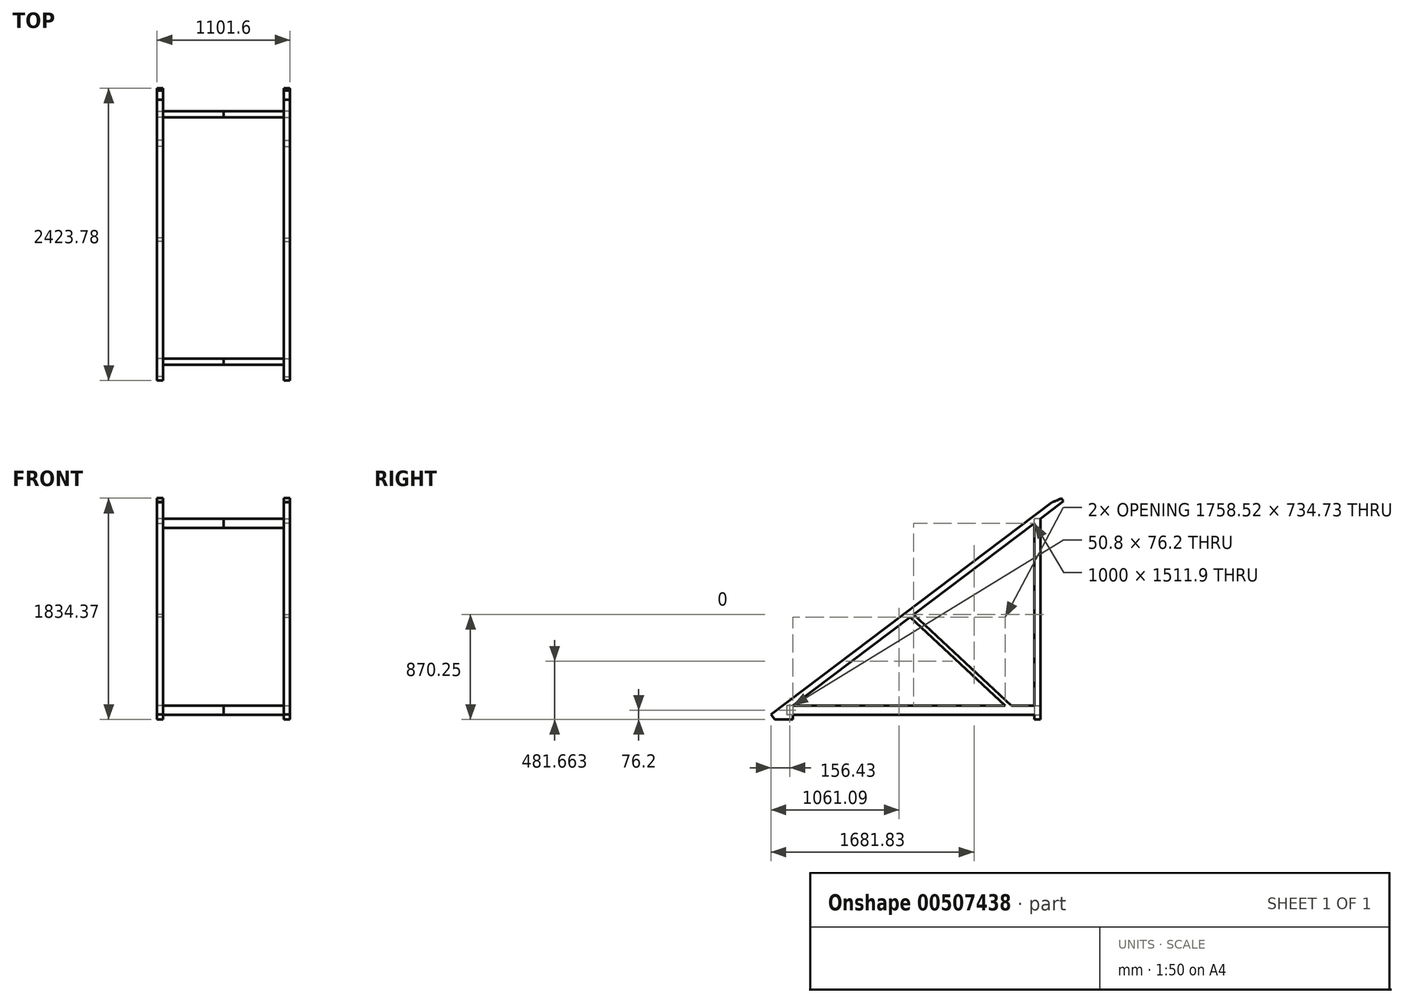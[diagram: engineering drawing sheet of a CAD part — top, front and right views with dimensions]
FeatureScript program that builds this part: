
annotation { "Feature Type Name" : "Feature", "Feature Type Description" : "" }
export const myFeature = defineFeature(function(context is Context, id is Id, definition is map)
    precondition{}
    {
        {
            var Q0;
            Q0=qCreatedBy(makeId("Front.planeOp"),FACE);
            var sketch = newSketch(context, id + "F0", { "sketchPlane" : qUnion([Q0])});
            skLineSegment(sketch, "E0.bottom", {"start": v(500, 0) * mm, "end": v(550.8, 0) * mm});
            skLineSegment(sketch, "E0.top", {"start": v(500, 76.2) * mm, "end": v(550.8, 76.2) * mm});
            skLineSegment(sketch, "E0.left", {"start": v(500, 0) * mm, "end": v(500, 76.2) * mm});
            skLineSegment(sketch, "E0.right", {"start": v(550.8, 0) * mm, "end": v(550.8, 76.2) * mm});
            skLineSegment(sketch, "E1", {"start": v(0, 0) * mm, "end": v(500, 0) * mm});
            skSolve(sketch);
        }
        {
            var Q0;
            Q0=qSketchRegion(id+"F0",true);
            extrude(context, id + "F1", {"entities" : qUnion([Q0]), "oppositeDirection" : true, "depth" : 2000 * mm});
        }
        {
            var Q0;
            Q0=makeQuery(id+"F1.opExtrude","CAP_FACE",FACE,{"disambiguationData":[OSD([sQuery(id+"F0.wireOp",EDGE,"E0.bottom"),sQuery(id+"F0.wireOp",EDGE,"E0.top"),sQuery(id+"F0.wireOp",EDGE,"E0.left"),sQuery(id+"F0.wireOp",EDGE,"E0.right")])],"isStart":false});
            var sketch = newSketch(context, id + "F2", { "sketchPlane" : qUnion([Q0])});
            skLineSegment(sketch, "E2", {"start": v(-550.8, 38.1) * mm, "end": v(-550.8, -38.1) * mm});
            skLineSegment(sketch, "E3", {"start": v(-550.8, -38.1) * mm, "end": v(-500, -38.1) * mm});
            skLineSegment(sketch, "E4", {"start": v(-500, -38.1) * mm, "end": v(-500, 38.1) * mm});
            skLineSegment(sketch, "E5.top", {"start": v(-550.8, 1588.1) * mm, "end": v(-500, 1588.1) * mm});
            skLineSegment(sketch, "E5.left", {"start": v(-550.8, 38.1) * mm, "end": v(-550.8, 1588.1) * mm});
            skLineSegment(sketch, "E5.right", {"start": v(-500, 38.1) * mm, "end": v(-500, 1588.1) * mm});
            skSolve(sketch);
        }
        {
            var Q0;
            Q0=qSketchRegion(id+"F2",true);
            extrude(context, id + "F3", {"entities" : qUnion([Q0]), "operationType" : NewBodyOperationType.ADD, "depth" : 50.8 * mm});
        }
        {
            var Q0;
            Q0=makeQuery(id+"F3.boolean.opBoolean","MERGE",FACE,{"derivedFrom":[makeQuery(id+"F1.opExtrude","SWEPT_FACE",FACE,{"disambiguationData":[OSD([sQuery(id+"F0.wireOp",EDGE,"E0.right")])]}),makeQuery(id+"F3.opExtrude","SWEPT_FACE",FACE,{"disambiguationData":[OSD([sQuery(id+"F2.wireOp",EDGE,"E2"),sQuery(id+"F2.wireOp",EDGE,"E5.left")])]})]});
            var sketch = newSketch(context, id + "F4", { "sketchPlane" : qUnion([Q0])});
            skLineSegment(sketch, "E6.0", {"start": v(2000, 76.2) * mm, "end": v(0, 76.2) * mm});
            skLineSegment(sketch, "E7.0", {"start": v(2000, 1588.1) * mm, "end": v(2000, 76.2) * mm});
            skLineSegment(sketch, "E8", {"start": v(-151.2, -38.1) * mm, "end": v(2241.95, 1771) * mm});
            skLineSegment(sketch, "E9", {"start": v(2241.95, 1771) * mm, "end": v(2000, 1588.1) * mm});
            skLineSegment(sketch, "E10.0", {"start": v(2050.8, -38.1) * mm, "end": v(2000, -38.1) * mm});
            skLineSegment(sketch, "E11", {"start": v(-151.2, -38.1) * mm, "end": v(0, -38.1) * mm});
            skPoint(sketch, "E12.0", {"position": v(2000, -19.05) * mm});
            skLineSegment(sketch, "E13.0", {"start": v(2000, 0) * mm, "end": v(2000, -38.1) * mm});
            skLineSegment(sketch, "E14", {"start": v(0, -38.1) * mm, "end": v(0, 0) * mm});
            skLineSegment(sketch, "E15", {"start": v(-151.2, -38.1) * mm, "end": v(-181.83, 2.42) * mm});
            skLineSegment(sketch, "E16", {"start": v(-181.83, 2.42) * mm, "end": v(2211.31, 1811.52) * mm});
            skLineSegment(sketch, "E17", {"start": v(2211.31, 1811.52) * mm, "end": v(2241.95, 1771) * mm});
            skLineSegment(sketch, "E18.0", {"start": v(2050.8, 1588.1) * mm, "end": v(2000, 1588.1) * mm});
            skLineSegment(sketch, "E19", {"start": v(2050.8, 1588.1) * mm, "end": v(2050.8, 1626.5) * mm});
            skSolve(sketch);
        }
        {
            var Q0;
            {var subQ0=sQuery(id+"F4.wireOp",EDGE,"E18.0");Q0=makeQuery(id+"F4.imprint","IMPRINT",FACE,{"disambiguationData":[TD([[makeQuery(id+"F4.imprint","IMPRINT",EDGE,{"derivedFrom":subQ0}),-1.0]])]});}
            var Q1;
            {var subQ6=sQuery(id+"F4.wireOp",EDGE,"E15");Q1=makeQuery(id+"F4.imprint","IMPRINT",FACE,{"disambiguationData":[TD([[makeQuery(id+"F4.imprint","IMPRINT",EDGE,{"derivedFrom":subQ6}),-1.0]])]});}
            var Q2;
            {var subQ2=sQuery(id+"F4.wireOp",EDGE,"E11");Q2=makeQuery(id+"F4.imprint","IMPRINT",FACE,{"disambiguationData":[TD([[makeQuery(id+"F4.imprint","IMPRINT",EDGE,{"derivedFrom":subQ2}),1.0]])]});}
            extrude(context, id + "F5", {"entities" : qUnion([Q0, Q1, Q2]), "operationType" : NewBodyOperationType.ADD, "oppositeDirection" : true, "depth" : 50.8 * mm});
        }
        {
            var Q0;
            Q0=makeQuery(id+"F5.boolean.opBoolean","MERGE",FACE,{"derivedFrom":[makeQuery(id+"F3.boolean.opBoolean","MERGE",FACE,{"derivedFrom":[makeQuery(id+"F1.opExtrude","SWEPT_FACE",FACE,{"disambiguationData":[OSD([sQuery(id+"F0.wireOp",EDGE,"E0.left")])]}),makeQuery(id+"F3.opExtrude","SWEPT_FACE",FACE,{"disambiguationData":[OSD([sQuery(id+"F2.wireOp",EDGE,"E4"),sQuery(id+"F2.wireOp",EDGE,"E5.right")])]})]}),makeQuery(id+"F5.opExtrude","CAP_FACE",FACE,{"disambiguationData":[OSD([sQuery(id+"F0.wireOp",EDGE,"E0.right"),sQuery(id+"F4.wireOp",EDGE,"E8"),sQuery(id+"F4.wireOp",EDGE,"E9"),sQuery(id+"F4.wireOp",EDGE,"E11"),sQuery(id+"F4.wireOp",EDGE,"E14"),sQuery(id+"F4.wireOp",EDGE,"E15"),sQuery(id+"F4.wireOp",EDGE,"E16"),sQuery(id+"F4.wireOp",EDGE,"E17"),sQuery(id+"F4.wireOp",EDGE,"E18.0"),sQuery(id+"F4.wireOp",EDGE,"E19")])],"isStart":false})]});
            var sketch = newSketch(context, id + "F6", { "sketchPlane" : qUnion([Q0])});
            skLineSegment(sketch, "E20.bottom", {"start": v(0, 76.2) * mm, "end": v(50.8, 76.2) * mm});
            skLineSegment(sketch, "E20.top", {"start": v(0, 0) * mm, "end": v(50.8, 0) * mm});
            skLineSegment(sketch, "E20.left", {"start": v(0, 76.2) * mm, "end": v(0, 0) * mm});
            skLineSegment(sketch, "E20.right", {"start": v(50.8, 76.2) * mm, "end": v(50.8, 0) * mm});
            skLineSegment(sketch, "E21.bottom", {"start": v(-2000, 76.2) * mm, "end": v(-2050.8, 76.2) * mm});
            skLineSegment(sketch, "E21.top", {"start": v(-2000, 0) * mm, "end": v(-2050.8, 0) * mm});
            skLineSegment(sketch, "E21.left", {"start": v(-2000, 76.2) * mm, "end": v(-2000, 0) * mm});
            skLineSegment(sketch, "E21.right", {"start": v(-2050.8, 76.2) * mm, "end": v(-2050.8, 0) * mm});
            skLineSegment(sketch, "E22.bottom", {"start": v(-2050.8, 1626.5) * mm, "end": v(-2000, 1626.5) * mm});
            skLineSegment(sketch, "E22.top", {"start": v(-2050.8, 1550.3) * mm, "end": v(-2000, 1550.3) * mm});
            skLineSegment(sketch, "E22.left", {"start": v(-2050.8, 1626.5) * mm, "end": v(-2050.8, 1550.3) * mm});
            skLineSegment(sketch, "E22.right", {"start": v(-2000, 1626.5) * mm, "end": v(-2000, 1550.3) * mm});
            skSolve(sketch);
        }
        {
            var Q0;
            Q0=qSketchRegion(id+"F6",true);
            extrude(context, id + "F7", {"entities" : qUnion([Q0]), "operationType" : NewBodyOperationType.ADD, "depth" : 500 * mm});
        }
        {
            var Q0;
            {var subQ0=makeQuery(id+"F7.boolean.opBoolean","MERGE",FACE,{"derivedFrom":[makeQuery(id+"F5.boolean.opBoolean","MERGE",FACE,{"derivedFrom":[makeQuery(id+"F3.opExtrude","CAP_FACE",FACE,{"disambiguationData":[OSD([sQuery(id+"F2.wireOp",EDGE,"E2"),sQuery(id+"F2.wireOp",EDGE,"E3"),sQuery(id+"F2.wireOp",EDGE,"E4"),sQuery(id+"F2.wireOp",EDGE,"E5.top"),sQuery(id+"F2.wireOp",EDGE,"E5.left"),sQuery(id+"F2.wireOp",EDGE,"E5.right")])],"isStart":false}),makeQuery(id+"F5.opExtrude","SWEPT_FACE",FACE,{"disambiguationData":[OSD([sQuery(id+"F4.wireOp",EDGE,"E19")])]})]}),makeQuery(id+"F7.opExtrude","SWEPT_FACE",FACE,{"disambiguationData":[OSD([sQuery(id+"F6.wireOp",EDGE,"E21.right")])]}),makeQuery(id+"F7.opExtrude","SWEPT_FACE",FACE,{"disambiguationData":[OSD([sQuery(id+"F6.wireOp",EDGE,"E22.left")])]})]});Q0=makeQuery(id+"F8JP7kFSM8YGR9G_1.boolean.opBoolean","MERGE",FACE,{"derivedFrom":[subQ0,makeQuery(id+"F8JP7kFSM8YGR9G_1.opPattern","COPY",FACE,{"derivedFrom":subQ0,"instanceName":"1"})]});}
            var sketch = newSketch(context, id + "F8", { "sketchPlane" : qUnion([Q0])});
            skLineSegment(sketch, "E23.0", {"start": v(-500, 76.2) * mm, "end": v(-500, 1550.3) * mm});
            skLineSegment(sketch, "E23.1", {"start": v(500, 1550.3) * mm, "end": v(-500, 1550.3) * mm});
            skLineSegment(sketch, "E23.2", {"start": v(500, 76.2) * mm, "end": v(500, 1550.3) * mm});
            skLineSegment(sketch, "E23.3", {"start": v(500, 76.2) * mm, "end": v(-500, 76.2) * mm});
            skLineSegment(sketch, "E24", {"start": v(-500, 1220.1) * mm, "end": v(500, 584.2) * mm});
            skLineSegment(sketch, "E25", {"start": v(-500, 584.2) * mm, "end": v(500, 1220.1) * mm});
            skLineSegment(sketch, "E26", {"start": v(-500, 1220.1) * mm, "end": v(-500, 1270.9) * mm});
            skLineSegment(sketch, "E27", {"start": v(-500, 1270.9) * mm, "end": v(500, 635) * mm});
            skLineSegment(sketch, "E28", {"start": v(500, 635) * mm, "end": v(500, 584.2) * mm});
            skLineSegment(sketch, "E29", {"start": v(-500, 584.2) * mm, "end": v(-500, 635) * mm});
            skLineSegment(sketch, "E30", {"start": v(-500, 635) * mm, "end": v(500, 1270.9) * mm});
            skLineSegment(sketch, "E31", {"start": v(500, 1270.9) * mm, "end": v(500, 1220.1) * mm});
            skLineSegment(sketch, "E32.0", {"start": v(550.8, 1626.5) * mm, "end": v(550.8, -38.1) * mm});
            skLineSegment(sketch, "E32.1", {"start": v(-550.8, 1626.5) * mm, "end": v(-550.8, -38.1) * mm});
            skSolve(sketch);
        }
        {
            var Q0;
            {var subQ0=sQuery(id+"F8.wireOp",EDGE,"E26");Q0=makeQuery(id+"F8.imprint","IMPRINT",FACE,{"disambiguationData":[TD([[makeQuery(id+"F8.imprint","IMPRINT",EDGE,{"derivedFrom":subQ0}),-1.0]])]});}
            var Q1;
            {var subQ5=sQuery(id+"F8.wireOp",EDGE,"E29");Q1=makeQuery(id+"F8.imprint","IMPRINT",FACE,{"disambiguationData":[TD([[makeQuery(id+"F8.imprint","IMPRINT",EDGE,{"derivedFrom":subQ5}),-1.0]])]});}
            var Q2;
            {var subQ0=sQuery(id+"F8.wireOp",EDGE,"E28");Q2=makeQuery(id+"F8.imprint","IMPRINT",FACE,{"disambiguationData":[TD([[makeQuery(id+"F8.imprint","IMPRINT",EDGE,{"derivedFrom":subQ0}),1.0]])]});}
            var Q3;
            {var subQ0=sQuery(id+"F8.wireOp",EDGE,"E31");Q3=makeQuery(id+"F8.imprint","IMPRINT",FACE,{"disambiguationData":[TD([[makeQuery(id+"F8.imprint","IMPRINT",EDGE,{"derivedFrom":subQ0}),1.0]])]});}
            var Q4;
            {var subQ0=sQuery(id+"F8.wireOp",EDGE,"E30");var subQ1=sQuery(id+"F8.wireOp",EDGE,"E24");var subQ2=makeQuery(id+"F8.imprint","INTERSECT",VERTEX,{"derivedFrom":[subQ1,subQ0]});Q4=makeQuery(id+"F8.imprint","IMPRINT",FACE,{"disambiguationData":[TD([[makeQuery(id+"F8.imprint","IMPRINT",EDGE,{"disambiguationData":[TD([[subQ2,-1.0]])],"derivedFrom":subQ1}),1.0]])]});}
            extrude(context, id + "F9", {"entities" : qUnion([Q0, Q1, Q2, Q3, Q4]), "oppositeDirection" : true, "depth" : 50.8 * mm});
        }
        {
            var Q0;
            {var subQ0=sQuery(id+"F0.wireOp",EDGE,"E0.right");Q0=makeQuery(id+"F5.boolean.opBoolean","MERGE",FACE,{"derivedFrom":[makeQuery(id+"F3.boolean.opBoolean","MERGE",FACE,{"derivedFrom":[makeQuery(id+"F1.opExtrude","SWEPT_FACE",FACE,{"disambiguationData":[OSD([subQ0])]}),makeQuery(id+"F3.opExtrude","SWEPT_FACE",FACE,{"disambiguationData":[OSD([sQuery(id+"F2.wireOp",EDGE,"E2"),sQuery(id+"F2.wireOp",EDGE,"E5.left")])]})]}),makeQuery(id+"F5.opExtrude","CAP_FACE",FACE,{"disambiguationData":[OSD([subQ0,sQuery(id+"F4.wireOp",EDGE,"E8"),sQuery(id+"F4.wireOp",EDGE,"E9"),sQuery(id+"F4.wireOp",EDGE,"E11"),sQuery(id+"F4.wireOp",EDGE,"E14"),sQuery(id+"F4.wireOp",EDGE,"E15"),sQuery(id+"F4.wireOp",EDGE,"E16"),sQuery(id+"F4.wireOp",EDGE,"E17"),sQuery(id+"F4.wireOp",EDGE,"E18.0"),sQuery(id+"F4.wireOp",EDGE,"E19")])],"isStart":true})]});}
            var sketch = newSketch(context, id + "F10", { "sketchPlane" : qUnion([Q0])});
            skLineSegment(sketch, "E33", {"start": v(2050.8, 1626.5) * mm, "end": v(2050.8, 1728.1) * mm, "construction": true});
            skArc(sketch, "E34", {"start": v(2386.46, 1978.93) * mm, "mid": v(2011.43, 1730.32) * mm, "end": v(1701.47, 2056.49) * mm});
            skLineSegment(sketch, "E35", {"start": v(2386.46, 1978.93) * mm, "end": v(2050.8, 2078.1) * mm, "construction": true});
            skLineSegment(sketch, "E36", {"start": v(1701.47, 2056.49) * mm, "end": v(2050.8, 2078.1) * mm, "construction": true});
            skArc(sketch, "E37", {"start": v(2367.47, 1984.54) * mm, "mid": v(2013.65, 1750) * mm, "end": v(1721.23, 2057.71) * mm});
            skLineSegment(sketch, "E38", {"start": v(1701.47, 2056.49) * mm, "end": v(1721.23, 2057.71) * mm});
            skLineSegment(sketch, "E39", {"start": v(2367.47, 1984.54) * mm, "end": v(2386.46, 1978.93) * mm});
            skSolve(sketch);
        }
        {
            var Q0;
            {var subQ0=sQuery(id+"F0.wireOp",EDGE,"E0.right");Q0=makeQuery(id+"FtUU4LHtogK7X8E_2.boolean.opBoolean","MERGE",FACE,{"derivedFrom":[makeQuery(id+"F5.boolean.opBoolean","MERGE",FACE,{"derivedFrom":[makeQuery(id+"F3.boolean.opBoolean","MERGE",FACE,{"derivedFrom":[makeQuery(id+"F1.opExtrude","SWEPT_FACE",FACE,{"disambiguationData":[OSD([subQ0])]}),makeQuery(id+"F3.opExtrude","SWEPT_FACE",FACE,{"disambiguationData":[OSD([sQuery(id+"F2.wireOp",EDGE,"E2"),sQuery(id+"F2.wireOp",EDGE,"E5.left")])]})]}),makeQuery(id+"F5.opExtrude","CAP_FACE",FACE,{"disambiguationData":[OSD([subQ0,sQuery(id+"F4.wireOp",EDGE,"E8"),sQuery(id+"F4.wireOp",EDGE,"E9"),sQuery(id+"F4.wireOp",EDGE,"E11"),sQuery(id+"F4.wireOp",EDGE,"E14"),sQuery(id+"F4.wireOp",EDGE,"E15"),sQuery(id+"F4.wireOp",EDGE,"E16"),sQuery(id+"F4.wireOp",EDGE,"E17"),sQuery(id+"F4.wireOp",EDGE,"E18.0"),sQuery(id+"F4.wireOp",EDGE,"E19")])],"isStart":true})]}),makeQuery(id+"FtUU4LHtogK7X8E_2.opExtrude","CAP_FACE",FACE,{"disambiguationData":[OSD([sQuery(id+"F10.wireOp",EDGE,"E34"),sQuery(id+"F10.wireOp",EDGE,"E37"),sQuery(id+"F10.wireOp",EDGE,"E38"),sQuery(id+"F10.wireOp",EDGE,"E39")])],"isStart":true})]});}
            var sketch = newSketch(context, id + "F11", { "sketchPlane" : qUnion([Q0])});
            skArc(sketch, "E40.0", {"start": v(2367.47, 1984.54) * mm, "mid": v(2013.65, 1750) * mm, "end": v(1721.23, 2057.71) * mm});
            skLineSegment(sketch, "E41.0", {"start": v(2145.5, 1761.77) * mm, "end": v(2211.31, 1811.52) * mm});
            skLineSegment(sketch, "E42.0", {"start": v(2211.31, 1811.52) * mm, "end": v(2222.85, 1796.27) * mm});
            skSolve(sketch);
        }
        {
            var Q0;
            Q0=qSketchRegion(id+"F11",true);
            extrude(context, id + "F12", {"entities" : qUnion([Q0]), "operationType" : NewBodyOperationType.REMOVE, "endBound" : BoundingType.THROUGH_ALL, "oppositeDirection" : true, "depth" : 25.4 * mm});
        }
        {
            var Q0;
            {var subQ0=sQuery(id+"F10.wireOp",EDGE,"E34");var subQ1=sQuery(id+"F0.wireOp",EDGE,"E0.right");Q0=makeQuery(id+"FoHvTBZFhzqH2Gp_2.boolean.opBoolean","MERGE",FACE,{"derivedFrom":[makeQuery(id+"FtUU4LHtogK7X8E_2.boolean.opBoolean","MERGE",FACE,{"derivedFrom":[makeQuery(id+"F5.boolean.opBoolean","MERGE",FACE,{"derivedFrom":[makeQuery(id+"F3.boolean.opBoolean","MERGE",FACE,{"derivedFrom":[makeQuery(id+"F1.opExtrude","SWEPT_FACE",FACE,{"disambiguationData":[OSD([subQ1])]}),makeQuery(id+"F3.opExtrude","SWEPT_FACE",FACE,{"disambiguationData":[OSD([sQuery(id+"F2.wireOp",EDGE,"E2"),sQuery(id+"F2.wireOp",EDGE,"E5.left")])]})]}),makeQuery(id+"F5.opExtrude","CAP_FACE",FACE,{"disambiguationData":[OSD([subQ1,sQuery(id+"F4.wireOp",EDGE,"E8"),sQuery(id+"F4.wireOp",EDGE,"E9"),sQuery(id+"F4.wireOp",EDGE,"E11"),sQuery(id+"F4.wireOp",EDGE,"E14"),sQuery(id+"F4.wireOp",EDGE,"E15"),sQuery(id+"F4.wireOp",EDGE,"E16"),sQuery(id+"F4.wireOp",EDGE,"E17"),sQuery(id+"F4.wireOp",EDGE,"E18.0"),sQuery(id+"F4.wireOp",EDGE,"E19")])],"isStart":true})]}),makeQuery(id+"FtUU4LHtogK7X8E_2.opExtrude","CAP_FACE",FACE,{"disambiguationData":[OSD([subQ0,sQuery(id+"F10.wireOp",EDGE,"E37"),sQuery(id+"F10.wireOp",EDGE,"E38"),sQuery(id+"F10.wireOp",EDGE,"E39")])],"isStart":true})]}),makeQuery(id+"FoHvTBZFhzqH2Gp_2.opExtrude","CAP_FACE",FACE,{"disambiguationData":[OSD([subQ0,sQuery(id+"F8mRdu26NR6OfP2_2.wireOp",EDGE,"8kur4JgX-Y46g-5CzW-4RUg-dFAypTCrmHBa"),sQuery(id+"F8mRdu26NR6OfP2_2.wireOp",EDGE,"ZUZMOovZ-q1vi-c5Jq-AADT-zK4e3nCVB9f8"),sQuery(id+"F8mRdu26NR6OfP2_2.wireOp",EDGE,"jsyQ2CFB-P6Mc-9hMs-pXjj-LjOdAAUgsXNg")])],"isStart":true})]});}
            var sketch = newSketch(context, id + "F13", { "sketchPlane" : qUnion([Q0])});
            skLineSegment(sketch, "E43", {"start": v(1809.32, 76.2) * mm, "end": v(1000, 832.15) * mm});
            skLineSegment(sketch, "E44", {"start": v(1000, 832.15) * mm, "end": v(971.92, 810.93) * mm});
            skLineSegment(sketch, "E45", {"start": v(971.92, 810.93) * mm, "end": v(1758.52, 76.2) * mm});
            skLineSegment(sketch, "E46", {"start": v(1758.52, 76.2) * mm, "end": v(1809.32, 76.2) * mm});
            skSolve(sketch);
        }
        {
            var Q0;
            Q0=qSketchRegion(id+"F13",true);
            extrude(context, id + "F14", {"entities" : qUnion([Q0]), "operationType" : NewBodyOperationType.ADD, "oppositeDirection" : true, "depth" : 50.8 * mm});
        }
        {
            var Q0;
            Q0=makeQuery(id+"F1.opExtrude","SWEPT_BODY",BODY,{"disambiguationData":[OSD([sQuery(id+"F0.wireOp",EDGE,"E0.bottom"),sQuery(id+"F0.wireOp",EDGE,"E0.top"),sQuery(id+"F0.wireOp",EDGE,"E0.left"),sQuery(id+"F0.wireOp",EDGE,"E0.right")])]});
            var Q1;
            Q1=makeQuery(id+"F9.opExtrude","SWEPT_BODY",BODY,{"disambiguationData":[OSD([sQuery(id+"F8.wireOp",EDGE,"E24"),sQuery(id+"F8.wireOp",EDGE,"E25"),sQuery(id+"F8.wireOp",EDGE,"E26"),sQuery(id+"F8.wireOp",EDGE,"E27"),sQuery(id+"F8.wireOp",EDGE,"E29"),sQuery(id+"F8.wireOp",EDGE,"E30")])]});
            var Q2;
            Q2=makeQuery(id+"F7.opExtrude","CAP_FACE",FACE,{"disambiguationData":[OSD([sQuery(id+"F6.wireOp",EDGE,"E21.bottom"),sQuery(id+"F6.wireOp",EDGE,"E21.top"),sQuery(id+"F6.wireOp",EDGE,"E21.left"),sQuery(id+"F6.wireOp",EDGE,"E21.right")])],"isStart":false});
            mirror(context, id + "F15", {"entities" : qUnion([Q0, Q1]), "mirrorPlane" : qUnion([Q2])});
        }
        {
            var Q0;
            Q0=makeQuery(id+"F15.opPattern","COPY",BODY,{"derivedFrom":makeQuery(id+"F9.opExtrude","SWEPT_BODY",BODY,{"disambiguationData":[OSD([sQuery(id+"F8.wireOp",EDGE,"E24"),sQuery(id+"F8.wireOp",EDGE,"E25"),sQuery(id+"F8.wireOp",EDGE,"E26"),sQuery(id+"F8.wireOp",EDGE,"E27"),sQuery(id+"F8.wireOp",EDGE,"E29"),sQuery(id+"F8.wireOp",EDGE,"E30")])]}),"instanceName":"1"});
            deleteBodies(context, id + "F16", {"entities" : qUnion([Q0])});
        }
        {
            var Q0;
            Q0=makeQuery(id+"F9.opExtrude","SWEPT_BODY",BODY,{"disambiguationData":[OSD([sQuery(id+"F8.wireOp",EDGE,"E24"),sQuery(id+"F8.wireOp",EDGE,"E25"),sQuery(id+"F8.wireOp",EDGE,"E26"),sQuery(id+"F8.wireOp",EDGE,"E27"),sQuery(id+"F8.wireOp",EDGE,"E29"),sQuery(id+"F8.wireOp",EDGE,"E30")])]});
            deleteBodies(context, id + "F17", {"entities" : qUnion([Q0])});
        }
    });
